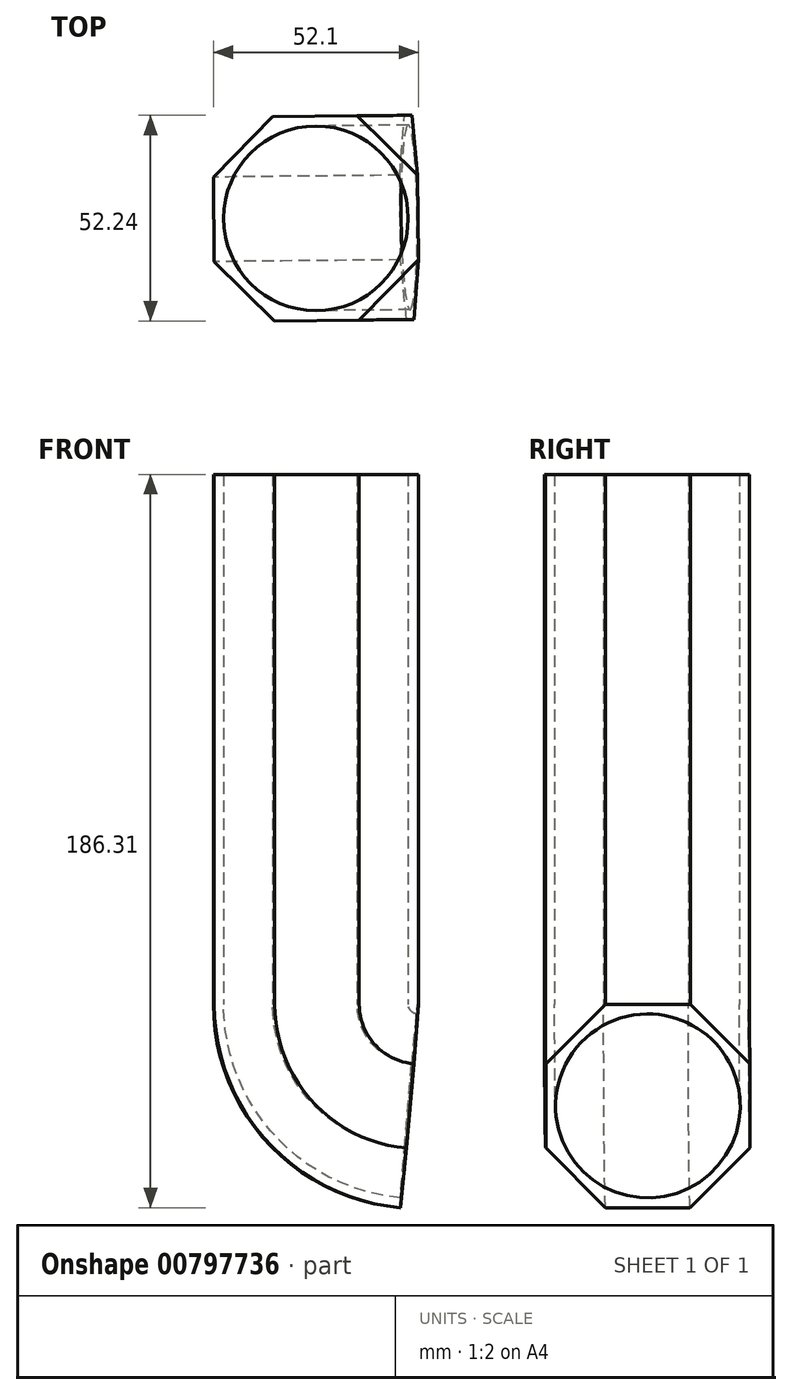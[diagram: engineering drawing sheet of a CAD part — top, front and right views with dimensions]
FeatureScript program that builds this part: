
annotation { "Feature Type Name" : "Feature", "Feature Type Description" : "" }
export const myFeature = defineFeature(function(context is Context, id is Id, definition is map)
    precondition{}
    {
        {
            var Q0;
            Q0=qCreatedBy(makeId("Top.planeOp"),FACE);
            var sketch = newSketch(context, id + "F0", { "sketchPlane" : qUnion([Q0])});
            skCircle(sketch, "E0.cCircle", {"center": v(0, 0) * mm, "radius": 25.94 * mm, "construction": true});
            skLineSegment(sketch, "E0.0", {"start": v(10.48, 26.05) * mm, "end": v(25.83, 11) * mm});
            skLineSegment(sketch, "E0.1", {"start": v(25.83, 11) * mm, "end": v(26.05, -10.48) * mm});
            skLineSegment(sketch, "E0.2", {"start": v(26.05, -10.48) * mm, "end": v(11, -25.83) * mm});
            skLineSegment(sketch, "E0.3", {"start": v(11, -25.83) * mm, "end": v(-10.48, -26.05) * mm});
            skLineSegment(sketch, "E0.4", {"start": v(-10.48, -26.05) * mm, "end": v(-25.83, -11) * mm});
            skLineSegment(sketch, "E0.5", {"start": v(-25.83, -11) * mm, "end": v(-26.05, 10.48) * mm});
            skLineSegment(sketch, "E0.6", {"start": v(-26.05, 10.48) * mm, "end": v(-11, 25.83) * mm});
            skLineSegment(sketch, "E0.7", {"start": v(-11, 25.83) * mm, "end": v(10.48, 26.05) * mm});
            skPoint(sketch, "E0.0.midPoint", {"position": v(18.16, 18.53) * mm});
            skCircle(sketch, "E1", {"center": v(0, 0) * mm, "radius": 23.45 * mm});
            skSolve(sketch);
        }
        {
            var Q0;
            Q0=makeQuery(id+"F0.imprint","IMPRINT",FACE,{"disambiguationData":[TD([[makeQuery(id+"F0.imprint","IMPRINT",EDGE,{"derivedFrom":sQuery(id+"F0.wireOp",EDGE,"E0.0")}),-1.0]])]});
            var Q1;
            Q1=sQuery(id+"F0.wireOp",EDGE,"E0.1");
            revolve(context, id + "F1", {"surfaceOperationType" : NewSurfaceOperationType.NEW, "entities" : qUnion([Q0]), "axis" : qUnion([Q1]), "revolveType" : RevolveType.ONE_DIRECTION, "angle" : 85 * degree});
        }
        {
            var Q0;
            Q0 = qSketchRegion(id + "F0", true);
            extrude(context, id + "F2", {"entities" : qUnion([Q0]), "operationType" : NewBodyOperationType.ADD, "depth" : 134.62 * mm, "offsetDistance" : 25.4 * mm});
        }
    });
